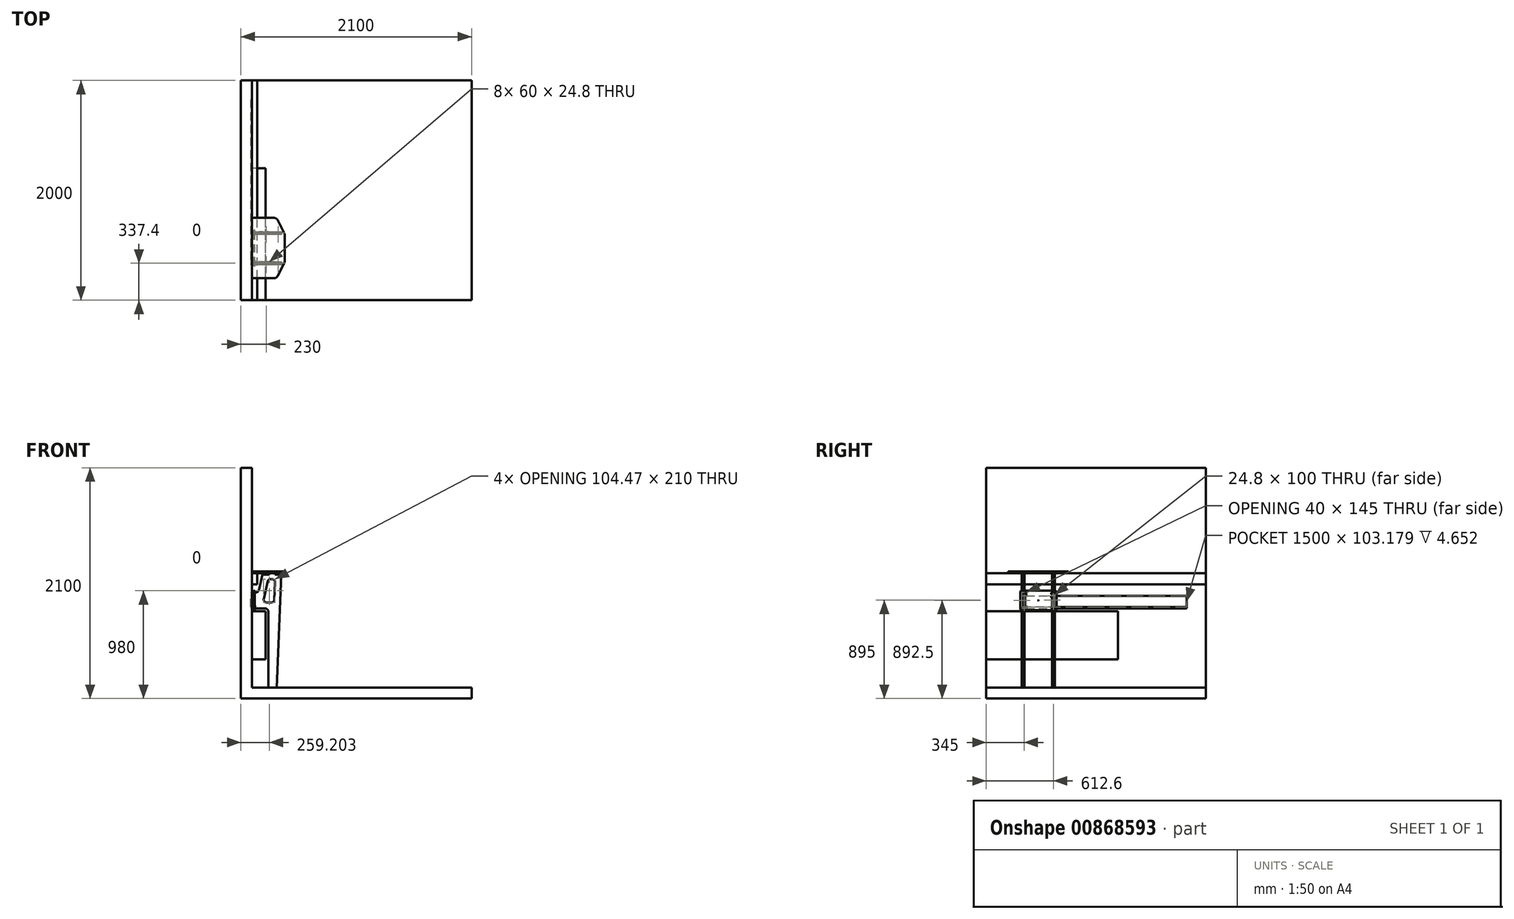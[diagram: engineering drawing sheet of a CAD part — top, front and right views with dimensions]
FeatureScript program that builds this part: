
annotation { "Feature Type Name" : "Feature", "Feature Type Description" : "" }
export const myFeature = defineFeature(function(context is Context, id is Id, definition is map)
    precondition{}
    {
        {
            var Q0;
            Q0=qCreatedBy(makeId("Front.planeOp"),FACE);
            var sketch = newSketch(context, id + "F0", { "sketchPlane" : qUnion([Q0])});
            skLineSegment(sketch, "E0", {"start": v(0, 2100) * mm, "end": v(0, 0) * mm});
            skLineSegment(sketch, "E1", {"start": v(0, 0) * mm, "end": v(2100, 0) * mm});
            skLineSegment(sketch, "E2", {"start": v(2100, 0) * mm, "end": v(2100, 100) * mm});
            skLineSegment(sketch, "E3", {"start": v(2100, 100) * mm, "end": v(100, 100) * mm});
            skLineSegment(sketch, "E4", {"start": v(100, 100) * mm, "end": v(100, 2100) * mm});
            skLineSegment(sketch, "E5", {"start": v(100, 2100) * mm, "end": v(0, 2100) * mm});
            skSolve(sketch);
        }
        {
            var Q0;
            Q0 = qSketchRegion(id + "F0", true);
            extrude(context, id + "F1", {"entities" : qUnion([Q0]), "depth" : 2000 * mm, "offsetDistance" : 25 * mm});
        }
        {
            var Q0;
            Q0=makeQuery(id+"F1.opExtrude","SWEPT_FACE",FACE,{"disambiguationData":[OSD([sQuery(id+"F0.wireOp",EDGE,"E4")])]});
            var sketch = newSketch(context, id + "F2", { "sketchPlane" : qUnion([Q0])});
            skLineSegment(sketch, "E6.bottom", {"start": v(-2000, 795) * mm, "end": v(-800, 795) * mm});
            skLineSegment(sketch, "E6.top", {"start": v(-2000, 355) * mm, "end": v(-800, 355) * mm});
            skLineSegment(sketch, "E6.left", {"start": v(-2000, 795) * mm, "end": v(-2000, 355) * mm});
            skLineSegment(sketch, "E6.right", {"start": v(-800, 795) * mm, "end": v(-800, 355) * mm});
            skSolve(sketch);
        }
        {
            var Q0;
            Q0 = qSketchRegion(id + "F2", true);
            extrude(context, id + "F3", {"entities" : qUnion([Q0]), "depth" : 125 * mm, "offsetDistance" : 25 * mm});
        }
        {
            var Q0;
            Q0=makeQuery(id+"F1.opExtrude","SWEPT_FACE",FACE,{"disambiguationData":[OSD([sQuery(id+"F0.wireOp",EDGE,"E4")])]});
            var sketch = newSketch(context, id + "F4", { "sketchPlane" : qUnion([Q0])});
            skLineSegment(sketch, "E7.bottom", {"start": v(-2000, 1140) * mm, "end": v(0, 1140) * mm});
            skLineSegment(sketch, "E7.top", {"start": v(-2000, 1040) * mm, "end": v(0, 1040) * mm});
            skLineSegment(sketch, "E7.left", {"start": v(-2000, 1140) * mm, "end": v(-2000, 1040) * mm});
            skLineSegment(sketch, "E7.right", {"start": v(0, 1140) * mm, "end": v(0, 1040) * mm});
            skSolve(sketch);
        }
        {
            var Q0;
            Q0 = qSketchRegion(id + "F4", true);
            extrude(context, id + "F5", {"entities" : qUnion([Q0]), "depth" : 50 * mm, "offsetDistance" : 25 * mm});
        }
        {
            var Q0;
            Q0=makeQuery(id+"F5.opExtrude","SWEPT_FACE",FACE,{"disambiguationData":[OSD([sQuery(id+"F4.wireOp",EDGE,"E7.bottom")])]});
            var sketch = newSketch(context, id + "F6", { "sketchPlane" : qUnion([Q0])});
            skLineSegment(sketch, "E8", {"start": v(100, -1800) * mm, "end": v(400, -1800) * mm});
            skLineSegment(sketch, "E9", {"start": v(400, -1800) * mm, "end": v(400, -1250) * mm});
            skLineSegment(sketch, "E10", {"start": v(400, -1250) * mm, "end": v(100, -1250) * mm});
            skLineSegment(sketch, "E11", {"start": v(100, -1250) * mm, "end": v(100, -1800) * mm});
            skSolve(sketch);
        }
        {
            var Q0;
            Q0 = qSketchRegion(id + "F6", true);
            extrude(context, id + "F7", {"entities" : qUnion([Q0]), "depth" : 6.2 * mm, "offsetDistance" : 25 * mm});
        }
        {
            var Q0;
            Q0=makeQuery(id+"F7.opExtrude","CAP_FACE",FACE,{"disambiguationData":[OSD([sQuery(id+"F6.wireOp",EDGE,"E8"),sQuery(id+"F6.wireOp",EDGE,"E9"),sQuery(id+"F6.wireOp",EDGE,"E10"),sQuery(id+"F6.wireOp",EDGE,"E11")])],"isStart":false});
            extrude(context, id + "F8", {"entities" : qUnion([Q0]), "depth" : 6.2 * mm, "offsetDistance" : 25 * mm});
        }
        {
            var Q0;
            Q0=makeQuery(id+"F8.opExtrude","SWEPT_EDGE",EDGE,{"disambiguationData":[OSD([sQuery(id+"F6.wireOp",EDGE,"E8"),sQuery(id+"F6.wireOp",EDGE,"E9")])]});
            var Q1;
            Q1=makeQuery(id+"F7.opExtrude","SWEPT_EDGE",EDGE,{"disambiguationData":[OSD([sQuery(id+"F6.wireOp",EDGE,"E8"),sQuery(id+"F6.wireOp",EDGE,"E9")])]});
            var Q2;
            Q2=makeQuery(id+"F8.opExtrude","SWEPT_EDGE",EDGE,{"disambiguationData":[OSD([sQuery(id+"F6.wireOp",EDGE,"E9"),sQuery(id+"F6.wireOp",EDGE,"E10")])]});
            var Q3;
            Q3=makeQuery(id+"F7.opExtrude","SWEPT_EDGE",EDGE,{"disambiguationData":[OSD([sQuery(id+"F6.wireOp",EDGE,"E9"),sQuery(id+"F6.wireOp",EDGE,"E10")])]});
            chamfer(context, id + "F9", {"entities" : qUnion([Q0, Q1, Q2, Q3]), "chamferType" : ChamferType.TWO_OFFSETS, "width1" : 150 * mm, "oppositeDirection" : false, "width2" : 75 * mm, "tangentPropagation" : true});
        }
        {
            var Q0;
            {var subQ0=sQuery(id+"F6.wireOp",EDGE,"E8");Q0=makeQuery(id+"F9.opChamfer","BLEND_EDGE",EDGE,{"blendedFrom":[makeQuery(id+"F8.opExtrude","SWEPT_EDGE",EDGE,{"disambiguationData":[OSD([subQ0,sQuery(id+"F6.wireOp",EDGE,"E9")])]}),makeQuery(id+"F8.opExtrude","SWEPT_FACE",FACE,{"disambiguationData":[OSD([subQ0])]})],"blendedInto":[makeQuery(id+"F8.opExtrude","SWEPT_FACE",FACE,{"disambiguationData":[OSD([subQ0])]})]});}
            var Q1;
            {var subQ0=sQuery(id+"F6.wireOp",EDGE,"E8");Q1=makeQuery(id+"F9.opChamfer","BLEND_EDGE",EDGE,{"blendedFrom":[makeQuery(id+"F7.opExtrude","SWEPT_EDGE",EDGE,{"disambiguationData":[OSD([subQ0,sQuery(id+"F6.wireOp",EDGE,"E9")])]}),makeQuery(id+"F7.opExtrude","SWEPT_FACE",FACE,{"disambiguationData":[OSD([subQ0])]})],"blendedInto":[makeQuery(id+"F7.opExtrude","SWEPT_FACE",FACE,{"disambiguationData":[OSD([subQ0])]})]});}
            var Q2;
            {var subQ0=sQuery(id+"F6.wireOp",EDGE,"E9");Q2=makeQuery(id+"F9.opChamfer","BLEND_EDGE",EDGE,{"blendedFrom":[makeQuery(id+"F8.opExtrude","SWEPT_EDGE",EDGE,{"disambiguationData":[OSD([sQuery(id+"F6.wireOp",EDGE,"E8"),subQ0])]}),makeQuery(id+"F8.opExtrude","SWEPT_FACE",FACE,{"disambiguationData":[OSD([subQ0])]})],"blendedInto":[makeQuery(id+"F8.opExtrude","SWEPT_FACE",FACE,{"disambiguationData":[OSD([subQ0])]})]});}
            var Q3;
            {var subQ0=sQuery(id+"F6.wireOp",EDGE,"E9");Q3=makeQuery(id+"F9.opChamfer","BLEND_EDGE",EDGE,{"blendedFrom":[makeQuery(id+"F7.opExtrude","SWEPT_EDGE",EDGE,{"disambiguationData":[OSD([sQuery(id+"F6.wireOp",EDGE,"E8"),subQ0])]}),makeQuery(id+"F7.opExtrude","SWEPT_FACE",FACE,{"disambiguationData":[OSD([subQ0])]})],"blendedInto":[makeQuery(id+"F7.opExtrude","SWEPT_FACE",FACE,{"disambiguationData":[OSD([subQ0])]})]});}
            var Q4;
            {var subQ0=sQuery(id+"F6.wireOp",EDGE,"E9");Q4=makeQuery(id+"F9.opChamfer","BLEND_EDGE",EDGE,{"blendedFrom":[makeQuery(id+"F8.opExtrude","SWEPT_EDGE",EDGE,{"disambiguationData":[OSD([subQ0,sQuery(id+"F6.wireOp",EDGE,"E10")])]}),makeQuery(id+"F8.opExtrude","SWEPT_FACE",FACE,{"disambiguationData":[OSD([subQ0])]})],"blendedInto":[makeQuery(id+"F8.opExtrude","SWEPT_FACE",FACE,{"disambiguationData":[OSD([subQ0])]})]});}
            var Q5;
            {var subQ0=sQuery(id+"F6.wireOp",EDGE,"E9");Q5=makeQuery(id+"F9.opChamfer","BLEND_EDGE",EDGE,{"blendedFrom":[makeQuery(id+"F7.opExtrude","SWEPT_EDGE",EDGE,{"disambiguationData":[OSD([subQ0,sQuery(id+"F6.wireOp",EDGE,"E10")])]}),makeQuery(id+"F7.opExtrude","SWEPT_FACE",FACE,{"disambiguationData":[OSD([subQ0])]})],"blendedInto":[makeQuery(id+"F7.opExtrude","SWEPT_FACE",FACE,{"disambiguationData":[OSD([subQ0])]})]});}
            var Q6;
            {var subQ0=sQuery(id+"F6.wireOp",EDGE,"E10");Q6=makeQuery(id+"F9.opChamfer","BLEND_EDGE",EDGE,{"blendedFrom":[makeQuery(id+"F8.opExtrude","SWEPT_EDGE",EDGE,{"disambiguationData":[OSD([sQuery(id+"F6.wireOp",EDGE,"E9"),subQ0])]}),makeQuery(id+"F8.opExtrude","SWEPT_FACE",FACE,{"disambiguationData":[OSD([subQ0])]})],"blendedInto":[makeQuery(id+"F8.opExtrude","SWEPT_FACE",FACE,{"disambiguationData":[OSD([subQ0])]})]});}
            var Q7;
            {var subQ0=sQuery(id+"F6.wireOp",EDGE,"E10");Q7=makeQuery(id+"F9.opChamfer","BLEND_EDGE",EDGE,{"blendedFrom":[makeQuery(id+"F7.opExtrude","SWEPT_EDGE",EDGE,{"disambiguationData":[OSD([sQuery(id+"F6.wireOp",EDGE,"E9"),subQ0])]}),makeQuery(id+"F7.opExtrude","SWEPT_FACE",FACE,{"disambiguationData":[OSD([subQ0])]})],"blendedInto":[makeQuery(id+"F7.opExtrude","SWEPT_FACE",FACE,{"disambiguationData":[OSD([subQ0])]})]});}
            fillet(context, id + "F10", {"entities" : qUnion([Q0, Q1, Q2, Q3, Q4, Q5, Q6, Q7]), "radius" : 40 * mm, "tangentPropagation" : true, "allowEdgeOverflow" : false});
        }
        {
            var Q0;
            Q0=makeQuery(id+"F8.opExtrude","CAP_FACE",FACE,{"disambiguationData":[OSD([sQuery(id+"F6.wireOp",EDGE,"E8"),sQuery(id+"F6.wireOp",EDGE,"E9"),sQuery(id+"F6.wireOp",EDGE,"E10"),sQuery(id+"F6.wireOp",EDGE,"E11")])],"isStart":false});
            extrude(context, id + "F11", {"entities" : qUnion([Q0]), "depth" : 4 * mm, "offsetDistance" : 25 * mm});
        }
        {
            var Q0;
            Q0=makeQuery(id+"F7.opExtrude","SWEPT_FACE",FACE,{"disambiguationData":[OSD([sQuery(id+"F6.wireOp",EDGE,"E8")])]});
            cPlane(context, id + "F12", {"entities" : qUnion([Q0]), "cplaneType" : CPlaneType.OFFSET, "offset" : 125 * mm, "oppositeDirection" : true, "width" : 150 * mm, "height" : 150 * mm});
        }
        {
            var Q0;
            Q0=makeQuery(id+"F8.opExtrude","SWEPT_FACE",FACE,{"disambiguationData":[OSD([sQuery(id+"F6.wireOp",EDGE,"E8")])]});
            var Q1;
            Q1=makeQuery(id+"F8.opExtrude","SWEPT_FACE",FACE,{"disambiguationData":[OSD([sQuery(id+"F6.wireOp",EDGE,"E10")])]});
            cPlane(context, id + "F13", {"entities" : qUnion([Q0, Q1]), "cplaneType" : CPlaneType.MID_PLANE, "offset" : 25 * mm, "width" : 150 * mm, "height" : 150 * mm});
        }
        {
            var Q0;
            Q0=qCreatedBy(id+"F12.planeOp",FACE);
            var sketch = newSketch(context, id + "F14", { "sketchPlane" : qUnion([Q0])});
            skLineSegment(sketch, "E12", {"start": v(200, 1152.4) * mm, "end": v(200, 1140) * mm});
            skLineSegment(sketch, "E13", {"start": v(200, 1140) * mm, "end": v(164.22, 988.12) * mm});
            skLineSegment(sketch, "E14", {"start": v(135.02, 965) * mm, "end": v(100, 965) * mm});
            skLineSegment(sketch, "E15", {"start": v(100, 965) * mm, "end": v(100, 820) * mm});
            skLineSegment(sketch, "E16", {"start": v(100, 820) * mm, "end": v(220, 820) * mm});
            skLineSegment(sketch, "E17", {"start": v(250, 790) * mm, "end": v(250, 100) * mm});
            skLineSegment(sketch, "E18", {"start": v(250, 100) * mm, "end": v(325, 100) * mm});
            skLineSegment(sketch, "E19", {"start": v(325, 100) * mm, "end": v(370, 1140) * mm});
            skLineSegment(sketch, "E20", {"start": v(370, 1140) * mm, "end": v(370, 1152.4) * mm});
            skLineSegment(sketch, "E21", {"start": v(370, 1152.4) * mm, "end": v(310, 1152.4) * mm});
            skPoint(sketch, "E22.visualSharp", {"position": v(250, 820) * mm});
            skArc(sketch, "E22.filletArc", {"start": v(250, 790) * mm, "mid": v(241.21, 811.21) * mm, "end": v(220, 820) * mm});
            skPoint(sketch, "E23.visualSharp", {"position": v(158.77, 965) * mm});
            skArc(sketch, "E23.filletArc", {"start": v(135.02, 965) * mm, "mid": v(153.64, 971.48) * mm, "end": v(164.22, 988.12) * mm});
            skLineSegment(sketch, "E24.top", {"start": v(260, 1140) * mm, "end": v(310, 1140) * mm});
            skLineSegment(sketch, "E24.left", {"start": v(260, 1152.4) * mm, "end": v(260, 1140) * mm});
            skLineSegment(sketch, "E24.right", {"start": v(310, 1152.4) * mm, "end": v(310, 1140) * mm});
            skLineSegment(sketch, "E25.trimOffspring", {"start": v(260, 1152.4) * mm, "end": v(200, 1152.4) * mm});
            skSolve(sketch);
        }
        {
            var Q0;
            Q0 = qSketchRegion(id + "F14", true);
            extrude(context, id + "F15", {"entities" : qUnion([Q0]), "oppositeDirection" : true, "depth" : 6.2 * mm, "offsetDistance" : 25 * mm});
        }
        {
            var Q0;
            Q0=makeQuery(id+"F15.opExtrude","SWEPT_BODY",BODY,{"disambiguationData":[OSD([sQuery(id+"F14.wireOp",EDGE,"E12"),sQuery(id+"F14.wireOp",EDGE,"E13"),sQuery(id+"F14.wireOp",EDGE,"E14"),sQuery(id+"F14.wireOp",EDGE,"E15"),sQuery(id+"F14.wireOp",EDGE,"E16"),sQuery(id+"F14.wireOp",EDGE,"E17"),sQuery(id+"F14.wireOp",EDGE,"E18"),sQuery(id+"F14.wireOp",EDGE,"E19"),sQuery(id+"F14.wireOp",EDGE,"E20"),sQuery(id+"F14.wireOp",EDGE,"E21"),sQuery(id+"F14.wireOp",EDGE,"E22.filletArc"),sQuery(id+"F14.wireOp",EDGE,"E23.filletArc"),sQuery(id+"F14.wireOp",EDGE,"E24.top"),sQuery(id+"F14.wireOp",EDGE,"E24.left"),sQuery(id+"F14.wireOp",EDGE,"E24.right"),sQuery(id+"F14.wireOp",EDGE,"E25.trimOffspring")])]});
            var Q1;
            Q1=makeQuery(id+"F15.opExtrude","CAP_FACE",FACE,{"disambiguationData":[OSD([sQuery(id+"F14.wireOp",EDGE,"E12"),sQuery(id+"F14.wireOp",EDGE,"E13"),sQuery(id+"F14.wireOp",EDGE,"E14"),sQuery(id+"F14.wireOp",EDGE,"E15"),sQuery(id+"F14.wireOp",EDGE,"E16"),sQuery(id+"F14.wireOp",EDGE,"E17"),sQuery(id+"F14.wireOp",EDGE,"E18"),sQuery(id+"F14.wireOp",EDGE,"E19"),sQuery(id+"F14.wireOp",EDGE,"E20"),sQuery(id+"F14.wireOp",EDGE,"E21"),sQuery(id+"F14.wireOp",EDGE,"E22.filletArc"),sQuery(id+"F14.wireOp",EDGE,"E23.filletArc"),sQuery(id+"F14.wireOp",EDGE,"E24.top"),sQuery(id+"F14.wireOp",EDGE,"E24.left"),sQuery(id+"F14.wireOp",EDGE,"E24.right"),sQuery(id+"F14.wireOp",EDGE,"E25.trimOffspring")])],"isStart":false});
            mirror(context, id + "F16", {"entities" : qUnion([Q0]), "mirrorPlane" : qUnion([Q1])});
        }
        {
            var Q0;
            Q0=makeQuery(id+"F15.opExtrude","SWEPT_BODY",BODY,{"disambiguationData":[OSD([sQuery(id+"F14.wireOp",EDGE,"E12"),sQuery(id+"F14.wireOp",EDGE,"E13"),sQuery(id+"F14.wireOp",EDGE,"E14"),sQuery(id+"F14.wireOp",EDGE,"E15"),sQuery(id+"F14.wireOp",EDGE,"E16"),sQuery(id+"F14.wireOp",EDGE,"E17"),sQuery(id+"F14.wireOp",EDGE,"E18"),sQuery(id+"F14.wireOp",EDGE,"E19"),sQuery(id+"F14.wireOp",EDGE,"E20"),sQuery(id+"F14.wireOp",EDGE,"E21"),sQuery(id+"F14.wireOp",EDGE,"E22.filletArc"),sQuery(id+"F14.wireOp",EDGE,"E23.filletArc"),sQuery(id+"F14.wireOp",EDGE,"E24.top"),sQuery(id+"F14.wireOp",EDGE,"E24.left"),sQuery(id+"F14.wireOp",EDGE,"E24.right"),sQuery(id+"F14.wireOp",EDGE,"E25.trimOffspring")])]});
            var Q1;
            Q1=makeQuery(id+"F16.opPattern","COPY",BODY,{"derivedFrom":makeQuery(id+"F15.opExtrude","SWEPT_BODY",BODY,{"disambiguationData":[OSD([sQuery(id+"F14.wireOp",EDGE,"E12"),sQuery(id+"F14.wireOp",EDGE,"E13"),sQuery(id+"F14.wireOp",EDGE,"E14"),sQuery(id+"F14.wireOp",EDGE,"E15"),sQuery(id+"F14.wireOp",EDGE,"E16"),sQuery(id+"F14.wireOp",EDGE,"E17"),sQuery(id+"F14.wireOp",EDGE,"E18"),sQuery(id+"F14.wireOp",EDGE,"E19"),sQuery(id+"F14.wireOp",EDGE,"E20"),sQuery(id+"F14.wireOp",EDGE,"E21"),sQuery(id+"F14.wireOp",EDGE,"E22.filletArc"),sQuery(id+"F14.wireOp",EDGE,"E23.filletArc"),sQuery(id+"F14.wireOp",EDGE,"E24.top"),sQuery(id+"F14.wireOp",EDGE,"E24.left"),sQuery(id+"F14.wireOp",EDGE,"E24.right"),sQuery(id+"F14.wireOp",EDGE,"E25.trimOffspring")])]}),"instanceName":"1"});
            var Q2;
            Q2=makeQuery(id+"F16.opPattern","COPY",FACE,{"derivedFrom":makeQuery(id+"F15.opExtrude","CAP_FACE",FACE,{"disambiguationData":[OSD([sQuery(id+"F14.wireOp",EDGE,"E12"),sQuery(id+"F14.wireOp",EDGE,"E13"),sQuery(id+"F14.wireOp",EDGE,"E14"),sQuery(id+"F14.wireOp",EDGE,"E15"),sQuery(id+"F14.wireOp",EDGE,"E16"),sQuery(id+"F14.wireOp",EDGE,"E17"),sQuery(id+"F14.wireOp",EDGE,"E18"),sQuery(id+"F14.wireOp",EDGE,"E19"),sQuery(id+"F14.wireOp",EDGE,"E20"),sQuery(id+"F14.wireOp",EDGE,"E21"),sQuery(id+"F14.wireOp",EDGE,"E22.filletArc"),sQuery(id+"F14.wireOp",EDGE,"E23.filletArc"),sQuery(id+"F14.wireOp",EDGE,"E24.top"),sQuery(id+"F14.wireOp",EDGE,"E24.left"),sQuery(id+"F14.wireOp",EDGE,"E24.right"),sQuery(id+"F14.wireOp",EDGE,"E25.trimOffspring")])],"isStart":true}),"instanceName":"1"});
            mirror(context, id + "F17", {"entities" : qUnion([Q0, Q1]), "mirrorPlane" : qUnion([Q2])});
        }
        {
            var Q0;
            Q0=makeQuery(id+"F15.opExtrude","SWEPT_BODY",BODY,{"disambiguationData":[OSD([sQuery(id+"F14.wireOp",EDGE,"E12"),sQuery(id+"F14.wireOp",EDGE,"E13"),sQuery(id+"F14.wireOp",EDGE,"E14"),sQuery(id+"F14.wireOp",EDGE,"E15"),sQuery(id+"F14.wireOp",EDGE,"E16"),sQuery(id+"F14.wireOp",EDGE,"E17"),sQuery(id+"F14.wireOp",EDGE,"E18"),sQuery(id+"F14.wireOp",EDGE,"E19"),sQuery(id+"F14.wireOp",EDGE,"E20"),sQuery(id+"F14.wireOp",EDGE,"E21"),sQuery(id+"F14.wireOp",EDGE,"E22.filletArc"),sQuery(id+"F14.wireOp",EDGE,"E23.filletArc"),sQuery(id+"F14.wireOp",EDGE,"E24.top"),sQuery(id+"F14.wireOp",EDGE,"E24.left"),sQuery(id+"F14.wireOp",EDGE,"E24.right"),sQuery(id+"F14.wireOp",EDGE,"E25.trimOffspring")])]});
            var Q1;
            Q1=makeQuery(id+"F16.opPattern","COPY",BODY,{"derivedFrom":makeQuery(id+"F15.opExtrude","SWEPT_BODY",BODY,{"disambiguationData":[OSD([sQuery(id+"F14.wireOp",EDGE,"E12"),sQuery(id+"F14.wireOp",EDGE,"E13"),sQuery(id+"F14.wireOp",EDGE,"E14"),sQuery(id+"F14.wireOp",EDGE,"E15"),sQuery(id+"F14.wireOp",EDGE,"E16"),sQuery(id+"F14.wireOp",EDGE,"E17"),sQuery(id+"F14.wireOp",EDGE,"E18"),sQuery(id+"F14.wireOp",EDGE,"E19"),sQuery(id+"F14.wireOp",EDGE,"E20"),sQuery(id+"F14.wireOp",EDGE,"E21"),sQuery(id+"F14.wireOp",EDGE,"E22.filletArc"),sQuery(id+"F14.wireOp",EDGE,"E23.filletArc"),sQuery(id+"F14.wireOp",EDGE,"E24.top"),sQuery(id+"F14.wireOp",EDGE,"E24.left"),sQuery(id+"F14.wireOp",EDGE,"E24.right"),sQuery(id+"F14.wireOp",EDGE,"E25.trimOffspring")])]}),"instanceName":"1"});
            var Q2;
            Q2=makeQuery(id+"F17.opPattern","COPY",BODY,{"derivedFrom":makeQuery(id+"F15.opExtrude","SWEPT_BODY",BODY,{"disambiguationData":[OSD([sQuery(id+"F14.wireOp",EDGE,"E12"),sQuery(id+"F14.wireOp",EDGE,"E13"),sQuery(id+"F14.wireOp",EDGE,"E14"),sQuery(id+"F14.wireOp",EDGE,"E15"),sQuery(id+"F14.wireOp",EDGE,"E16"),sQuery(id+"F14.wireOp",EDGE,"E17"),sQuery(id+"F14.wireOp",EDGE,"E18"),sQuery(id+"F14.wireOp",EDGE,"E19"),sQuery(id+"F14.wireOp",EDGE,"E20"),sQuery(id+"F14.wireOp",EDGE,"E21"),sQuery(id+"F14.wireOp",EDGE,"E22.filletArc"),sQuery(id+"F14.wireOp",EDGE,"E23.filletArc"),sQuery(id+"F14.wireOp",EDGE,"E24.top"),sQuery(id+"F14.wireOp",EDGE,"E24.left"),sQuery(id+"F14.wireOp",EDGE,"E24.right"),sQuery(id+"F14.wireOp",EDGE,"E25.trimOffspring")])]}),"instanceName":"1"});
            var Q3;
            Q3=makeQuery(id+"F17.opPattern","COPY",BODY,{"derivedFrom":makeQuery(id+"F16.opPattern","COPY",BODY,{"derivedFrom":makeQuery(id+"F15.opExtrude","SWEPT_BODY",BODY,{"disambiguationData":[OSD([sQuery(id+"F14.wireOp",EDGE,"E12"),sQuery(id+"F14.wireOp",EDGE,"E13"),sQuery(id+"F14.wireOp",EDGE,"E14"),sQuery(id+"F14.wireOp",EDGE,"E15"),sQuery(id+"F14.wireOp",EDGE,"E16"),sQuery(id+"F14.wireOp",EDGE,"E17"),sQuery(id+"F14.wireOp",EDGE,"E18"),sQuery(id+"F14.wireOp",EDGE,"E19"),sQuery(id+"F14.wireOp",EDGE,"E20"),sQuery(id+"F14.wireOp",EDGE,"E21"),sQuery(id+"F14.wireOp",EDGE,"E22.filletArc"),sQuery(id+"F14.wireOp",EDGE,"E23.filletArc"),sQuery(id+"F14.wireOp",EDGE,"E24.top"),sQuery(id+"F14.wireOp",EDGE,"E24.left"),sQuery(id+"F14.wireOp",EDGE,"E24.right"),sQuery(id+"F14.wireOp",EDGE,"E25.trimOffspring")])]}),"instanceName":"1"}),"instanceName":"1"});
            var Q4;
            Q4=qCreatedBy(id+"F13.planeOp",FACE);
            mirror(context, id + "F18", {"entities" : qUnion([Q0, Q1, Q2, Q3]), "mirrorPlane" : qUnion([Q4])});
        }
        {
            var Q0;
            Q0=makeQuery(id+"F1.opExtrude","SWEPT_FACE",FACE,{"disambiguationData":[OSD([sQuery(id+"F0.wireOp",EDGE,"E4")])]});
            cPlane(context, id + "F19", {"entities" : qUnion([Q0]), "cplaneType" : CPlaneType.OFFSET, "offset" : 20 * mm, "width" : 150 * mm, "height" : 150 * mm});
        }
        {
            var Q0;
            Q0=qCreatedBy(id+"F19.planeOp",FACE);
            var sketch = newSketch(context, id + "F20", { "sketchPlane" : qUnion([Q0])});
            skLineSegment(sketch, "E26.bottom", {"start": v(-1690, 980) * mm, "end": v(-1360, 980) * mm});
            skLineSegment(sketch, "E26.top", {"start": v(-1690, 805) * mm, "end": v(-1360, 805) * mm});
            skLineSegment(sketch, "E26.left", {"start": v(-1690, 980) * mm, "end": v(-1690, 805) * mm});
            skLineSegment(sketch, "E26.right", {"start": v(-1360, 980) * mm, "end": v(-1360, 805) * mm});
            skLineSegment(sketch, "E27.bottom", {"start": v(-1675, 945) * mm, "end": v(-1650.2, 945) * mm});
            skLineSegment(sketch, "E27.top", {"start": v(-1675, 845) * mm, "end": v(-1650.2, 845) * mm});
            skLineSegment(sketch, "E27.left", {"start": v(-1675, 945) * mm, "end": v(-1675, 845) * mm});
            skLineSegment(sketch, "E27.right", {"start": v(-1650.2, 945) * mm, "end": v(-1650.2, 845) * mm});
            skLineSegment(sketch, "E28", {"start": v(-1525, 980) * mm, "end": v(-1525, 884.43) * mm, "construction": true});
            skLineSegment(sketch, "E29.MirrorCS", {"start": v(-1375, 945) * mm, "end": v(-1399.8, 945) * mm});
            skLineSegment(sketch, "E30.MirrorCS", {"start": v(-1375, 945) * mm, "end": v(-1375, 845) * mm});
            skLineSegment(sketch, "E31.MirrorCS", {"start": v(-1375, 845) * mm, "end": v(-1399.8, 845) * mm});
            skLineSegment(sketch, "E32.MirrorCS", {"start": v(-1399.8, 945) * mm, "end": v(-1399.8, 845) * mm});
            skSolve(sketch);
        }
        {
            var Q0;
            Q0 = qSketchRegion(id + "F20", true);
            extrude(context, id + "F21", {"entities" : qUnion([Q0]), "depth" : 6.2 * mm, "offsetDistance" : 25 * mm});
        }
        {
            var Q0;
            Q0=makeQuery(id+"F21.opExtrude","SWEPT_EDGE",EDGE,{"disambiguationData":[OSD([sQuery(id+"F20.wireOp",EDGE,"E26.bottom"),sQuery(id+"F20.wireOp",EDGE,"E26.left")])]});
            var Q1;
            Q1=makeQuery(id+"F21.opExtrude","SWEPT_EDGE",EDGE,{"disambiguationData":[OSD([sQuery(id+"F20.wireOp",EDGE,"E26.top"),sQuery(id+"F20.wireOp",EDGE,"E26.left")])]});
            var Q2;
            Q2=makeQuery(id+"F21.opExtrude","SWEPT_EDGE",EDGE,{"disambiguationData":[OSD([sQuery(id+"F20.wireOp",EDGE,"E26.bottom"),sQuery(id+"F20.wireOp",EDGE,"E26.right")])]});
            var Q3;
            Q3=makeQuery(id+"F21.opExtrude","SWEPT_EDGE",EDGE,{"disambiguationData":[OSD([sQuery(id+"F20.wireOp",EDGE,"E26.top"),sQuery(id+"F20.wireOp",EDGE,"E26.right")])]});
            fillet(context, id + "F22", {"entities" : qUnion([Q0, Q1, Q2, Q3]), "radius" : 10 * mm, "tangentPropagation" : true, "allowEdgeOverflow" : false});
        }
        {
            var Q0;
            Q0=makeQuery(id+"F15.opExtrude","CAP_FACE",FACE,{"disambiguationData":[OSD([sQuery(id+"F14.wireOp",EDGE,"E12"),sQuery(id+"F14.wireOp",EDGE,"E13"),sQuery(id+"F14.wireOp",EDGE,"E14"),sQuery(id+"F14.wireOp",EDGE,"E15"),sQuery(id+"F14.wireOp",EDGE,"E16"),sQuery(id+"F14.wireOp",EDGE,"E17"),sQuery(id+"F14.wireOp",EDGE,"E18"),sQuery(id+"F14.wireOp",EDGE,"E19"),sQuery(id+"F14.wireOp",EDGE,"E20"),sQuery(id+"F14.wireOp",EDGE,"E21"),sQuery(id+"F14.wireOp",EDGE,"E22.filletArc"),sQuery(id+"F14.wireOp",EDGE,"E23.filletArc"),sQuery(id+"F14.wireOp",EDGE,"E24.top"),sQuery(id+"F14.wireOp",EDGE,"E24.left"),sQuery(id+"F14.wireOp",EDGE,"E24.right"),sQuery(id+"F14.wireOp",EDGE,"E25.trimOffspring")])],"isStart":true});
            var sketch = newSketch(context, id + "F23", { "sketchPlane" : qUnion([Q0])});
            skLineSegment(sketch, "E33", {"start": v(100, 930) * mm, "end": v(126.2, 930) * mm});
            skLineSegment(sketch, "E34", {"start": v(126.2, 930) * mm, "end": v(126.2, 965) * mm});
            skLineSegment(sketch, "E35", {"start": v(126.2, 965) * mm, "end": v(91.31, 965) * mm});
            skLineSegment(sketch, "E36", {"start": v(91.31, 965) * mm, "end": v(100, 930) * mm});
            skLineSegment(sketch, "E37.bottom", {"start": v(120, 820) * mm, "end": v(129, 820) * mm});
            skLineSegment(sketch, "E37.top", {"start": v(120, 845) * mm, "end": v(129, 845) * mm});
            skLineSegment(sketch, "E37.left", {"start": v(120, 820) * mm, "end": v(120, 845) * mm});
            skLineSegment(sketch, "E37.right", {"start": v(129, 820) * mm, "end": v(129, 845) * mm});
            skSolve(sketch);
        }
        {
            var Q0;
            Q0 = qSketchRegion(id + "F23", true);
            extrude(context, id + "F24", {"entities" : qUnion([Q0]), "operationType" : NewBodyOperationType.REMOVE, "oppositeDirection" : true, "depth" : 40 * mm, "offsetDistance" : 25 * mm});
        }
        {
            var Q0;
            {var subQ0=sQuery(id+"F14.wireOp",EDGE,"E25.trimOffspring");var subQ1=sQuery(id+"F14.wireOp",EDGE,"E24.right");var subQ2=sQuery(id+"F14.wireOp",EDGE,"E24.left");var subQ3=sQuery(id+"F14.wireOp",EDGE,"E24.top");var subQ4=sQuery(id+"F14.wireOp",EDGE,"E23.filletArc");var subQ5=sQuery(id+"F14.wireOp",EDGE,"E22.filletArc");var subQ6=sQuery(id+"F14.wireOp",EDGE,"E21");var subQ7=sQuery(id+"F14.wireOp",EDGE,"E20");var subQ8=sQuery(id+"F14.wireOp",EDGE,"E19");var subQ9=sQuery(id+"F14.wireOp",EDGE,"E18");var subQ10=sQuery(id+"F14.wireOp",EDGE,"E17");var subQ11=sQuery(id+"F14.wireOp",EDGE,"E16");var subQ12=sQuery(id+"F14.wireOp",EDGE,"E15");var subQ13=sQuery(id+"F14.wireOp",EDGE,"E14");var subQ14=sQuery(id+"F14.wireOp",EDGE,"E13");var subQ15=sQuery(id+"F14.wireOp",EDGE,"E12");var subQ16=sQuery(id+"F23.wireOp",EDGE,"E37.top");var subQ17=sQuery(id+"F23.wireOp",EDGE,"E37.right");Q0=makeQuery(id+"F24.boolean.opBoolean","COPY",EDGE,{"disambiguationData":[TD([makeQuery(id+"F15.opExtrude","CAP_FACE",FACE,{"disambiguationData":[OSD([subQ15,subQ14,subQ13,subQ12,subQ11,subQ10,subQ9,subQ8,subQ7,subQ6,subQ5,subQ4,subQ3,subQ2,subQ1,subQ0])],"isStart":true})])],"derivedFrom":makeQuery(id+"F24.opExtrude","SWEPT_EDGE",EDGE,{"disambiguationData":[OSD([subQ16,subQ17])]})});}
            var Q1;
            {var subQ0=sQuery(id+"F14.wireOp",EDGE,"E25.trimOffspring");var subQ1=sQuery(id+"F14.wireOp",EDGE,"E24.right");var subQ2=sQuery(id+"F14.wireOp",EDGE,"E24.left");var subQ3=sQuery(id+"F14.wireOp",EDGE,"E24.top");var subQ4=sQuery(id+"F14.wireOp",EDGE,"E23.filletArc");var subQ5=sQuery(id+"F14.wireOp",EDGE,"E22.filletArc");var subQ6=sQuery(id+"F14.wireOp",EDGE,"E21");var subQ7=sQuery(id+"F14.wireOp",EDGE,"E20");var subQ8=sQuery(id+"F14.wireOp",EDGE,"E19");var subQ9=sQuery(id+"F14.wireOp",EDGE,"E18");var subQ10=sQuery(id+"F14.wireOp",EDGE,"E17");var subQ11=sQuery(id+"F14.wireOp",EDGE,"E16");var subQ12=sQuery(id+"F14.wireOp",EDGE,"E15");var subQ13=sQuery(id+"F14.wireOp",EDGE,"E14");var subQ14=sQuery(id+"F14.wireOp",EDGE,"E13");var subQ15=sQuery(id+"F14.wireOp",EDGE,"E12");var subQ16=sQuery(id+"F23.wireOp",EDGE,"E37.top");var subQ17=sQuery(id+"F23.wireOp",EDGE,"E37.right");Q1=makeQuery(id+"F24.boolean.opBoolean","COPY",EDGE,{"disambiguationData":[TD([makeQuery(id+"F16.opPattern","COPY",FACE,{"derivedFrom":makeQuery(id+"F15.opExtrude","CAP_FACE",FACE,{"disambiguationData":[OSD([subQ15,subQ14,subQ13,subQ12,subQ11,subQ10,subQ9,subQ8,subQ7,subQ6,subQ5,subQ4,subQ3,subQ2,subQ1,subQ0])],"isStart":true}),"instanceName":"1"})])],"derivedFrom":makeQuery(id+"F24.opExtrude","SWEPT_EDGE",EDGE,{"disambiguationData":[OSD([subQ16,subQ17])]})});}
            var Q2;
            {var subQ0=sQuery(id+"F14.wireOp",EDGE,"E25.trimOffspring");var subQ1=sQuery(id+"F14.wireOp",EDGE,"E24.right");var subQ2=sQuery(id+"F14.wireOp",EDGE,"E24.left");var subQ3=sQuery(id+"F14.wireOp",EDGE,"E24.top");var subQ4=sQuery(id+"F14.wireOp",EDGE,"E23.filletArc");var subQ5=sQuery(id+"F14.wireOp",EDGE,"E22.filletArc");var subQ6=sQuery(id+"F14.wireOp",EDGE,"E21");var subQ7=sQuery(id+"F14.wireOp",EDGE,"E20");var subQ8=sQuery(id+"F14.wireOp",EDGE,"E19");var subQ9=sQuery(id+"F14.wireOp",EDGE,"E18");var subQ10=sQuery(id+"F14.wireOp",EDGE,"E17");var subQ11=sQuery(id+"F14.wireOp",EDGE,"E16");var subQ12=sQuery(id+"F14.wireOp",EDGE,"E15");var subQ13=sQuery(id+"F14.wireOp",EDGE,"E14");var subQ14=sQuery(id+"F14.wireOp",EDGE,"E13");var subQ15=sQuery(id+"F14.wireOp",EDGE,"E12");var subQ16=sQuery(id+"F23.wireOp",EDGE,"E37.top");var subQ17=sQuery(id+"F23.wireOp",EDGE,"E37.right");Q2=makeQuery(id+"F24.boolean.opBoolean","COPY",EDGE,{"disambiguationData":[TD([makeQuery(id+"F17.opPattern","COPY",FACE,{"derivedFrom":makeQuery(id+"F16.opPattern","COPY",FACE,{"derivedFrom":makeQuery(id+"F15.opExtrude","CAP_FACE",FACE,{"disambiguationData":[OSD([subQ15,subQ14,subQ13,subQ12,subQ11,subQ10,subQ9,subQ8,subQ7,subQ6,subQ5,subQ4,subQ3,subQ2,subQ1,subQ0])],"isStart":true}),"instanceName":"1"}),"instanceName":"1"})])],"derivedFrom":makeQuery(id+"F24.opExtrude","SWEPT_EDGE",EDGE,{"disambiguationData":[OSD([subQ16,subQ17])]})});}
            var Q3;
            {var subQ0=sQuery(id+"F14.wireOp",EDGE,"E25.trimOffspring");var subQ1=sQuery(id+"F14.wireOp",EDGE,"E24.right");var subQ2=sQuery(id+"F14.wireOp",EDGE,"E24.left");var subQ3=sQuery(id+"F14.wireOp",EDGE,"E24.top");var subQ4=sQuery(id+"F14.wireOp",EDGE,"E23.filletArc");var subQ5=sQuery(id+"F14.wireOp",EDGE,"E22.filletArc");var subQ6=sQuery(id+"F14.wireOp",EDGE,"E21");var subQ7=sQuery(id+"F14.wireOp",EDGE,"E20");var subQ8=sQuery(id+"F14.wireOp",EDGE,"E19");var subQ9=sQuery(id+"F14.wireOp",EDGE,"E18");var subQ10=sQuery(id+"F14.wireOp",EDGE,"E17");var subQ11=sQuery(id+"F14.wireOp",EDGE,"E16");var subQ12=sQuery(id+"F14.wireOp",EDGE,"E15");var subQ13=sQuery(id+"F14.wireOp",EDGE,"E14");var subQ14=sQuery(id+"F14.wireOp",EDGE,"E13");var subQ15=sQuery(id+"F14.wireOp",EDGE,"E12");var subQ16=sQuery(id+"F23.wireOp",EDGE,"E37.top");var subQ17=sQuery(id+"F23.wireOp",EDGE,"E37.right");Q3=makeQuery(id+"F24.boolean.opBoolean","COPY",EDGE,{"disambiguationData":[TD([makeQuery(id+"F17.opPattern","COPY",FACE,{"derivedFrom":makeQuery(id+"F15.opExtrude","CAP_FACE",FACE,{"disambiguationData":[OSD([subQ15,subQ14,subQ13,subQ12,subQ11,subQ10,subQ9,subQ8,subQ7,subQ6,subQ5,subQ4,subQ3,subQ2,subQ1,subQ0])],"isStart":true}),"instanceName":"1"})])],"derivedFrom":makeQuery(id+"F24.opExtrude","SWEPT_EDGE",EDGE,{"disambiguationData":[OSD([subQ16,subQ17])]})});}
            fillet(context, id + "F25", {"entities" : qUnion([Q0, Q1, Q2, Q3]), "radius" : 3 * mm, "tangentPropagation" : true, "allowEdgeOverflow" : false});
        }
        {
            var Q0;
            {var subQ0=sQuery(id+"F14.wireOp",EDGE,"E16");var subQ1=sQuery(id+"F23.wireOp",EDGE,"E37.right");Q0=makeQuery(id+"F24.boolean.opBoolean","COPY",EDGE,{"disambiguationData":[topologyDisambiguationEdgeConnected([makeQuery(id+"F17.opPattern","COPY",FACE,{"derivedFrom":makeQuery(id+"F15.opExtrude","SWEPT_FACE",FACE,{"disambiguationData":[OSD([subQ0])]}),"instanceName":"1"})])],"derivedFrom":makeQuery(id+"F24.opExtrude","SWEPT_EDGE",EDGE,{"disambiguationData":[OSD([subQ0,sQuery(id+"F23.wireOp",EDGE,"E37.bottom"),subQ1])]})});}
            var Q1;
            {var subQ0=sQuery(id+"F14.wireOp",EDGE,"E16");var subQ1=sQuery(id+"F23.wireOp",EDGE,"E37.right");Q1=makeQuery(id+"F24.boolean.opBoolean","COPY",EDGE,{"disambiguationData":[topologyDisambiguationEdgeConnected([makeQuery(id+"F17.opPattern","COPY",FACE,{"derivedFrom":makeQuery(id+"F16.opPattern","COPY",FACE,{"derivedFrom":makeQuery(id+"F15.opExtrude","SWEPT_FACE",FACE,{"disambiguationData":[OSD([subQ0])]}),"instanceName":"1"}),"instanceName":"1"})])],"derivedFrom":makeQuery(id+"F24.opExtrude","SWEPT_EDGE",EDGE,{"disambiguationData":[OSD([subQ0,sQuery(id+"F23.wireOp",EDGE,"E37.bottom"),subQ1])]})});}
            var Q2;
            {var subQ0=sQuery(id+"F14.wireOp",EDGE,"E16");var subQ1=sQuery(id+"F23.wireOp",EDGE,"E37.right");Q2=makeQuery(id+"F24.boolean.opBoolean","COPY",EDGE,{"disambiguationData":[topologyDisambiguationEdgeConnected([makeQuery(id+"F16.opPattern","COPY",FACE,{"derivedFrom":makeQuery(id+"F15.opExtrude","SWEPT_FACE",FACE,{"disambiguationData":[OSD([subQ0])]}),"instanceName":"1"})])],"derivedFrom":makeQuery(id+"F24.opExtrude","SWEPT_EDGE",EDGE,{"disambiguationData":[OSD([subQ0,sQuery(id+"F23.wireOp",EDGE,"E37.bottom"),subQ1])]})});}
            var Q3;
            {var subQ0=sQuery(id+"F14.wireOp",EDGE,"E16");var subQ1=sQuery(id+"F23.wireOp",EDGE,"E37.right");Q3=makeQuery(id+"F24.boolean.opBoolean","COPY",EDGE,{"disambiguationData":[topologyDisambiguationEdgeConnected([makeQuery(id+"F15.opExtrude","SWEPT_FACE",FACE,{"disambiguationData":[OSD([subQ0])]})])],"derivedFrom":makeQuery(id+"F24.opExtrude","SWEPT_EDGE",EDGE,{"disambiguationData":[OSD([subQ0,sQuery(id+"F23.wireOp",EDGE,"E37.bottom"),subQ1])]})});}
            var Q4;
            {var subQ0=sQuery(id+"F14.wireOp",EDGE,"E15");var subQ1=sQuery(id+"F23.wireOp",EDGE,"E33");Q4=makeQuery(id+"F24.boolean.opBoolean","COPY",EDGE,{"disambiguationData":[topologyDisambiguationEdgeConnected([makeQuery(id+"F15.opExtrude","SWEPT_FACE",FACE,{"disambiguationData":[OSD([subQ0])]})])],"derivedFrom":makeQuery(id+"F24.opExtrude","SWEPT_EDGE",EDGE,{"disambiguationData":[OSD([subQ0,subQ1,sQuery(id+"F23.wireOp",EDGE,"E36")])]})});}
            var Q5;
            {var subQ0=sQuery(id+"F14.wireOp",EDGE,"E15");var subQ1=sQuery(id+"F23.wireOp",EDGE,"E33");Q5=makeQuery(id+"F24.boolean.opBoolean","COPY",EDGE,{"disambiguationData":[topologyDisambiguationEdgeConnected([makeQuery(id+"F16.opPattern","COPY",FACE,{"derivedFrom":makeQuery(id+"F15.opExtrude","SWEPT_FACE",FACE,{"disambiguationData":[OSD([subQ0])]}),"instanceName":"1"})])],"derivedFrom":makeQuery(id+"F24.opExtrude","SWEPT_EDGE",EDGE,{"disambiguationData":[OSD([subQ0,subQ1,sQuery(id+"F23.wireOp",EDGE,"E36")])]})});}
            var Q6;
            {var subQ0=sQuery(id+"F14.wireOp",EDGE,"E15");var subQ1=sQuery(id+"F23.wireOp",EDGE,"E33");Q6=makeQuery(id+"F24.boolean.opBoolean","COPY",EDGE,{"disambiguationData":[topologyDisambiguationEdgeConnected([makeQuery(id+"F17.opPattern","COPY",FACE,{"derivedFrom":makeQuery(id+"F16.opPattern","COPY",FACE,{"derivedFrom":makeQuery(id+"F15.opExtrude","SWEPT_FACE",FACE,{"disambiguationData":[OSD([subQ0])]}),"instanceName":"1"}),"instanceName":"1"})])],"derivedFrom":makeQuery(id+"F24.opExtrude","SWEPT_EDGE",EDGE,{"disambiguationData":[OSD([subQ0,subQ1,sQuery(id+"F23.wireOp",EDGE,"E36")])]})});}
            var Q7;
            {var subQ0=sQuery(id+"F14.wireOp",EDGE,"E15");var subQ1=sQuery(id+"F23.wireOp",EDGE,"E33");Q7=makeQuery(id+"F24.boolean.opBoolean","COPY",EDGE,{"disambiguationData":[topologyDisambiguationEdgeConnected([makeQuery(id+"F17.opPattern","COPY",FACE,{"derivedFrom":makeQuery(id+"F15.opExtrude","SWEPT_FACE",FACE,{"disambiguationData":[OSD([subQ0])]}),"instanceName":"1"})])],"derivedFrom":makeQuery(id+"F24.opExtrude","SWEPT_EDGE",EDGE,{"disambiguationData":[OSD([subQ0,subQ1,sQuery(id+"F23.wireOp",EDGE,"E36")])]})});}
            var Q8;
            Q8=makeQuery(id+"F17.opPattern","COPY",EDGE,{"derivedFrom":makeQuery(id+"F15.opExtrude","SWEPT_EDGE",EDGE,{"disambiguationData":[OSD([sQuery(id+"F14.wireOp",EDGE,"E15"),sQuery(id+"F14.wireOp",EDGE,"E16")])]}),"instanceName":"1"});
            var Q9;
            Q9=makeQuery(id+"F17.opPattern","COPY",EDGE,{"derivedFrom":makeQuery(id+"F16.opPattern","COPY",EDGE,{"derivedFrom":makeQuery(id+"F15.opExtrude","SWEPT_EDGE",EDGE,{"disambiguationData":[OSD([sQuery(id+"F14.wireOp",EDGE,"E15"),sQuery(id+"F14.wireOp",EDGE,"E16")])]}),"instanceName":"1"}),"instanceName":"1"});
            var Q10;
            Q10=makeQuery(id+"F16.opPattern","COPY",EDGE,{"derivedFrom":makeQuery(id+"F15.opExtrude","SWEPT_EDGE",EDGE,{"disambiguationData":[OSD([sQuery(id+"F14.wireOp",EDGE,"E15"),sQuery(id+"F14.wireOp",EDGE,"E16")])]}),"instanceName":"1"});
            var Q11;
            Q11=makeQuery(id+"F15.opExtrude","SWEPT_EDGE",EDGE,{"disambiguationData":[OSD([sQuery(id+"F14.wireOp",EDGE,"E15"),sQuery(id+"F14.wireOp",EDGE,"E16")])]});
            fillet(context, id + "F26", {"entities" : qUnion([Q0, Q1, Q2, Q3, Q4, Q5, Q6, Q7, Q8, Q9, Q10, Q11]), "radius" : 2 * mm, "tangentPropagation" : true, "allowEdgeOverflow" : false});
        }
        {
            var Q0;
            Q0=makeQuery(id+"F21.opExtrude","CAP_FACE",FACE,{"disambiguationData":[OSD([sQuery(id+"F20.wireOp",EDGE,"E26.bottom"),sQuery(id+"F20.wireOp",EDGE,"E26.top"),sQuery(id+"F20.wireOp",EDGE,"E26.left"),sQuery(id+"F20.wireOp",EDGE,"E26.right"),sQuery(id+"F20.wireOp",EDGE,"E27.bottom"),sQuery(id+"F20.wireOp",EDGE,"E27.top"),sQuery(id+"F20.wireOp",EDGE,"E27.left"),sQuery(id+"F20.wireOp",EDGE,"E27.right"),sQuery(id+"F20.wireOp",EDGE,"E29.MirrorCS"),sQuery(id+"F20.wireOp",EDGE,"E30.MirrorCS"),sQuery(id+"F20.wireOp",EDGE,"E31.MirrorCS"),sQuery(id+"F20.wireOp",EDGE,"E32.MirrorCS")])],"isStart":false});
            var sketch = newSketch(context, id + "F27", { "sketchPlane" : qUnion([Q0])});
            skCircle(sketch, "E38", {"center": v(-1640.2, 955) * mm, "radius": 1.75 * mm});
            skCircle(sketch, "E39", {"center": v(-1640.2, 830) * mm, "radius": 1.75 * mm});
            skCircle(sketch, "E40", {"center": v(-1640.2, 925) * mm, "radius": 1.75 * mm});
            skLineSegment(sketch, "E41", {"start": v(-1525, 980) * mm, "end": v(-1525, 805) * mm, "construction": true});
            skCircle(sketch, "E42", {"center": v(-1525, 892.5) * mm, "radius": 1.75 * mm});
            skCircle(sketch, "E43.MirrorC", {"center": v(-1409.8, 925) * mm, "radius": 1.75 * mm});
            skCircle(sketch, "E44.MirrorC", {"center": v(-1409.8, 955) * mm, "radius": 1.75 * mm});
            skCircle(sketch, "E45.MirrorC", {"center": v(-1409.8, 830) * mm, "radius": 1.75 * mm});
            skSolve(sketch);
        }
        {
            var Q0;
            Q0 = qSketchRegion(id + "F27", true);
            extrude(context, id + "F28", {"entities" : qUnion([Q0]), "operationType" : NewBodyOperationType.REMOVE, "oppositeDirection" : true, "depth" : 25 * mm, "offsetDistance" : 25 * mm});
        }
        {
            var Q0;
            Q0=makeQuery(id+"F8.opExtrude","CAP_FACE",FACE,{"disambiguationData":[OSD([sQuery(id+"F6.wireOp",EDGE,"E8"),sQuery(id+"F6.wireOp",EDGE,"E9"),sQuery(id+"F6.wireOp",EDGE,"E10"),sQuery(id+"F6.wireOp",EDGE,"E11")])],"isStart":false});
            var sketch = newSketch(context, id + "F29", { "sketchPlane" : qUnion([Q0])});
            skLineSegment(sketch, "E46.bottom", {"start": v(200, -1375) * mm, "end": v(260, -1375) * mm});
            skLineSegment(sketch, "E46.top", {"start": v(200, -1399.8) * mm, "end": v(260, -1399.8) * mm});
            skLineSegment(sketch, "E46.left", {"start": v(200, -1375) * mm, "end": v(200, -1399.8) * mm});
            skLineSegment(sketch, "E46.right", {"start": v(260, -1375) * mm, "end": v(260, -1399.8) * mm});
            skLineSegment(sketch, "E47.bottom", {"start": v(310, -1375) * mm, "end": v(370, -1375) * mm});
            skLineSegment(sketch, "E47.top", {"start": v(310, -1399.8) * mm, "end": v(370, -1399.8) * mm});
            skLineSegment(sketch, "E47.left", {"start": v(310, -1375) * mm, "end": v(310, -1399.8) * mm});
            skLineSegment(sketch, "E47.right", {"start": v(370, -1375) * mm, "end": v(370, -1399.8) * mm});
            skLineSegment(sketch, "E48.bottom", {"start": v(200, -1650.2) * mm, "end": v(260, -1650.2) * mm});
            skLineSegment(sketch, "E48.top", {"start": v(200, -1675) * mm, "end": v(260, -1675) * mm});
            skLineSegment(sketch, "E48.left", {"start": v(200, -1650.2) * mm, "end": v(200, -1675) * mm});
            skLineSegment(sketch, "E48.right", {"start": v(260, -1650.2) * mm, "end": v(260, -1675) * mm});
            skLineSegment(sketch, "E49.bottom", {"start": v(310, -1650.2) * mm, "end": v(370, -1650.2) * mm});
            skLineSegment(sketch, "E49.top", {"start": v(310, -1675) * mm, "end": v(370, -1675) * mm});
            skLineSegment(sketch, "E49.left", {"start": v(310, -1650.2) * mm, "end": v(310, -1675) * mm});
            skLineSegment(sketch, "E49.right", {"start": v(370, -1650.2) * mm, "end": v(370, -1675) * mm});
            skSolve(sketch);
        }
        {
            var Q0;
            Q0 = qSketchRegion(id + "F29", true);
            extrude(context, id + "F30", {"entities" : qUnion([Q0]), "operationType" : NewBodyOperationType.REMOVE, "oppositeDirection" : true, "depth" : 25 * mm, "offsetDistance" : 25 * mm});
        }
        {
            var Q0;
            Q0=makeQuery(id+"F15.opExtrude","CAP_FACE",FACE,{"disambiguationData":[OSD([sQuery(id+"F14.wireOp",EDGE,"E12"),sQuery(id+"F14.wireOp",EDGE,"E13"),sQuery(id+"F14.wireOp",EDGE,"E14"),sQuery(id+"F14.wireOp",EDGE,"E15"),sQuery(id+"F14.wireOp",EDGE,"E16"),sQuery(id+"F14.wireOp",EDGE,"E17"),sQuery(id+"F14.wireOp",EDGE,"E18"),sQuery(id+"F14.wireOp",EDGE,"E19"),sQuery(id+"F14.wireOp",EDGE,"E20"),sQuery(id+"F14.wireOp",EDGE,"E21"),sQuery(id+"F14.wireOp",EDGE,"E22.filletArc"),sQuery(id+"F14.wireOp",EDGE,"E23.filletArc"),sQuery(id+"F14.wireOp",EDGE,"E24.top"),sQuery(id+"F14.wireOp",EDGE,"E24.left"),sQuery(id+"F14.wireOp",EDGE,"E24.right"),sQuery(id+"F14.wireOp",EDGE,"E25.trimOffspring")])],"isStart":true});
            var sketch = newSketch(context, id + "F31", { "sketchPlane" : qUnion([Q0])});
            skLineSegment(sketch, "E50.bottom", {"start": v(120, 820) * mm, "end": v(94, 820) * mm});
            skLineSegment(sketch, "E50.top", {"start": v(120, 832) * mm, "end": v(107, 832) * mm});
            skLineSegment(sketch, "E50.left", {"start": v(120, 820) * mm, "end": v(120, 832) * mm});
            skLineSegment(sketch, "E50.right", {"start": v(94, 820) * mm, "end": v(94, 832) * mm});
            skLineSegment(sketch, "E51.bottom", {"start": v(94, 832) * mm, "end": v(89.35, 832) * mm});
            skLineSegment(sketch, "E51.top", {"start": v(107, 935.18) * mm, "end": v(89.35, 935.18) * mm});
            skLineSegment(sketch, "E51.left", {"start": v(107, 832) * mm, "end": v(107, 935.18) * mm});
            skLineSegment(sketch, "E51.right", {"start": v(89.35, 832) * mm, "end": v(89.35, 935.18) * mm});
            skSolve(sketch);
        }
        {
            var Q0;
            Q0 = qSketchRegion(id + "F31", true);
            extrude(context, id + "F32", {"entities" : qUnion([Q0]), "operationType" : NewBodyOperationType.REMOVE, "oppositeDirection" : true, "depth" : 1500 * mm, "offsetDistance" : 25 * mm});
        }
        {
            var Q0;
            Q0=makeQuery(id+"F32.boolean.opBoolean","COPY",EDGE,{"derivedFrom":makeQuery(id+"F32.opExtrude","SWEPT_EDGE",EDGE,{"disambiguationData":[OSD([sQuery(id+"F31.wireOp",EDGE,"E50.top"),sQuery(id+"F31.wireOp",EDGE,"E51.left")])]})});
            fillet(context, id + "F33", {"entities" : qUnion([Q0]), "radius" : 2 * mm, "tangentPropagation" : true, "allowEdgeOverflow" : false});
        }
        {
            var Q0;
            Q0=makeQuery(id+"F15.opExtrude","CAP_FACE",FACE,{"disambiguationData":[OSD([sQuery(id+"F14.wireOp",EDGE,"E12"),sQuery(id+"F14.wireOp",EDGE,"E13"),sQuery(id+"F14.wireOp",EDGE,"E14"),sQuery(id+"F14.wireOp",EDGE,"E15"),sQuery(id+"F14.wireOp",EDGE,"E16"),sQuery(id+"F14.wireOp",EDGE,"E17"),sQuery(id+"F14.wireOp",EDGE,"E18"),sQuery(id+"F14.wireOp",EDGE,"E19"),sQuery(id+"F14.wireOp",EDGE,"E20"),sQuery(id+"F14.wireOp",EDGE,"E21"),sQuery(id+"F14.wireOp",EDGE,"E22.filletArc"),sQuery(id+"F14.wireOp",EDGE,"E23.filletArc"),sQuery(id+"F14.wireOp",EDGE,"E24.top"),sQuery(id+"F14.wireOp",EDGE,"E24.left"),sQuery(id+"F14.wireOp",EDGE,"E24.right"),sQuery(id+"F14.wireOp",EDGE,"E25.trimOffspring")])],"isStart":true});
            var sketch = newSketch(context, id + "F34", { "sketchPlane" : qUnion([Q0])});
            skLineSegment(sketch, "E52.0", {"start": v(304.52, 898.92) * mm, "end": v(311.44, 1058.92) * mm});
            skLineSegment(sketch, "E53", {"start": v(231.97, 875) * mm, "end": v(279.54, 875) * mm});
            skLineSegment(sketch, "E54", {"start": v(242.9, 1065.4) * mm, "end": v(207.55, 905.4) * mm});
            skLineSegment(sketch, "E55", {"start": v(267.3, 1085) * mm, "end": v(286.46, 1085) * mm});
            skPoint(sketch, "E56.visualSharp", {"position": v(247.22, 1085) * mm});
            skArc(sketch, "E56.filletArc", {"start": v(267.3, 1085) * mm, "mid": v(251.65, 1079.5) * mm, "end": v(242.9, 1065.4) * mm});
            skPoint(sketch, "E57.visualSharp", {"position": v(312.57, 1085) * mm});
            skArc(sketch, "E57.filletArc", {"start": v(311.44, 1058.92) * mm, "mid": v(304.52, 1077.3) * mm, "end": v(286.46, 1085) * mm});
            skPoint(sketch, "E58.visualSharp", {"position": v(303.48, 875) * mm});
            skArc(sketch, "E58.filletArc", {"start": v(279.54, 875) * mm, "mid": v(296.83, 881.94) * mm, "end": v(304.52, 898.92) * mm});
            skPoint(sketch, "E59.visualSharp", {"position": v(200.84, 875) * mm});
            skArc(sketch, "E59.filletArc", {"start": v(207.55, 905.4) * mm, "mid": v(212.47, 884.34) * mm, "end": v(231.97, 875) * mm});
            skSolve(sketch);
        }
        {
            var Q0;
            Q0 = qSketchRegion(id + "F34", true);
            extrude(context, id + "F35", {"entities" : qUnion([Q0]), "operationType" : NewBodyOperationType.REMOVE, "oppositeDirection" : true, "depth" : 25 * mm, "offsetDistance" : 25 * mm});
        }
    });
